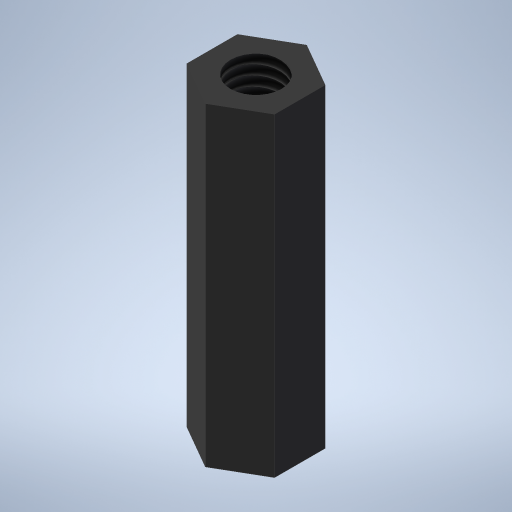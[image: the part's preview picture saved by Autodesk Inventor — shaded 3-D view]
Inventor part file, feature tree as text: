
AUTODESK INVENTOR PART (.ipt)
format: ipt  version: 2024 (Build 280153000, 153)  size: 225,792 bytes
history: native  units: in
note: dims shown in document units (in); Inventor stores cm internally (conversion verified against a paired STEP export)
features: extrude x2, sketch x2, thread x1
ambient origin geometry x8: Origin, YZ Plane, XZ Plane, XY Plane, X Axis, Y Axis, Z Axis, Center Point
bodies: Solid1 (feature_tree)
feature tree (5):
  extrude  "Extrusion1"  Depth=1.793in TaperAngle=0.0deg
  extrude  "Extrusion2"  Depth=1.793in TaperAngle=0.0deg
  thread  "Thread1"  [1 undecoded]
  sketch  "Sketch1"  dims[d0=0.5in d1=1.793in d2=0.0in]
  sketch  "Sketch2"  dims[d3=0.291in d4=1.793in d5=0.0in d6=1.793in d7=0.0in]
note: 1 required parameter value undecoded (feature->parameter linkage not recoverable at this tier; creation-order binding heuristic only, values carry confidence <= 0.55)
